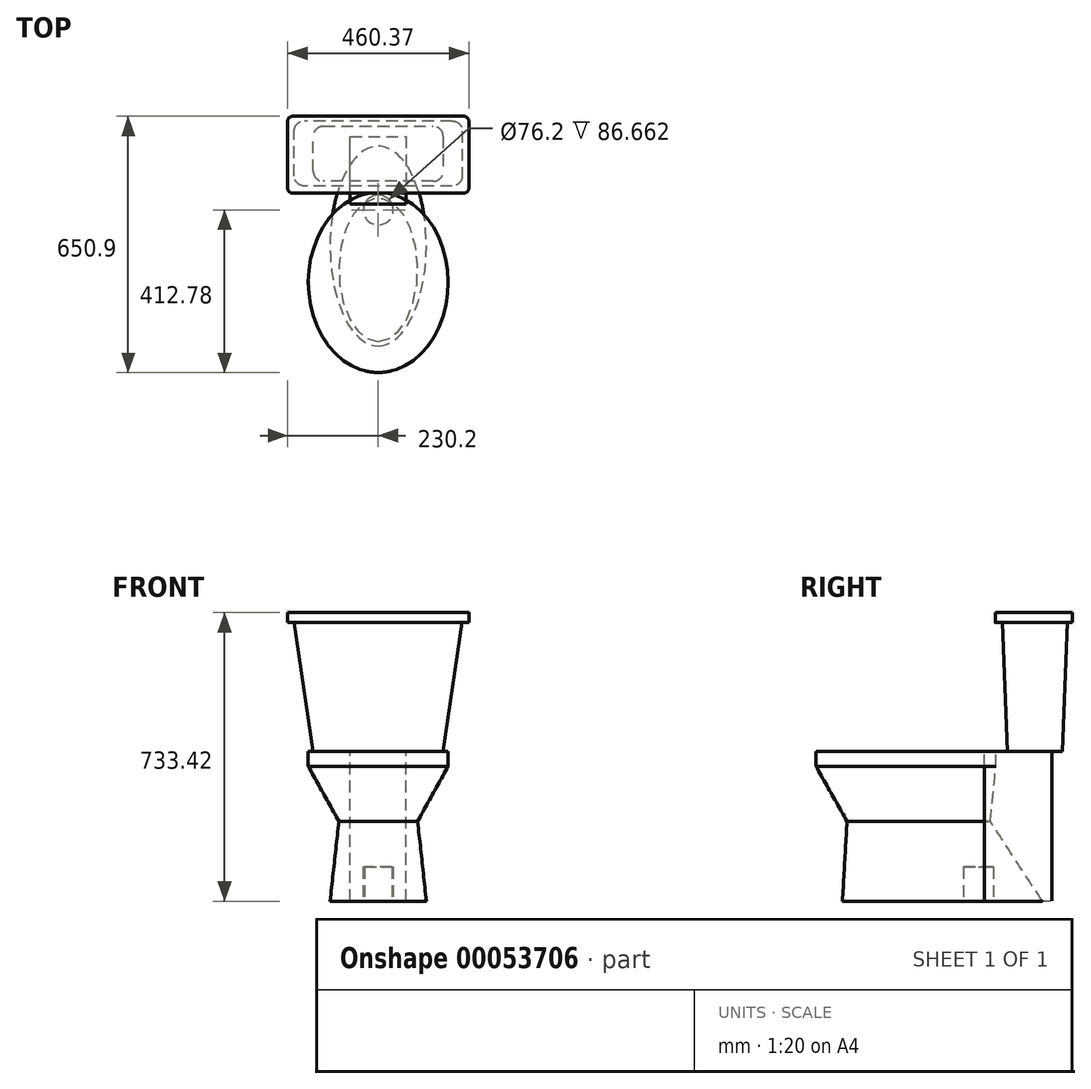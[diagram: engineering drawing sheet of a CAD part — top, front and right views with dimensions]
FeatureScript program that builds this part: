
annotation { "Feature Type Name" : "Feature", "Feature Type Description" : "" }
export const myFeature = defineFeature(function(context is Context, id is Id, definition is map)
    precondition{}
    {
        {
            var Q0;
            Q0=qCreatedBy(makeId("Top.planeOp"),FACE);
            var sketch = newSketch(context, id + "F0", { "sketchPlane" : qUnion([Q0])});
            skEllipse(sketch, "E0", {"center": v(0, 0) * mm, "majorRadius": 254 * mm, "minorRadius": 122.24 * mm, "majorAxis": v(0, 1)});
            skSolve(sketch);
        }
        {
            var Q0;
            Q0=makeQuery(id+"F0.imprint","IMPRINT",FACE,{"disambiguationData":[TD([[makeQuery(id+"F0.imprint","IMPRINT",EDGE,{"derivedFrom":sQuery(id+"F0.wireOp",EDGE,"E0")}),1.0]])]});
            cPlane(context, id + "F1", {"entities" : qUnion([Q0]), "cplaneType" : CPlaneType.OFFSET, "offset" : 203.2 * mm, "width" : 152.4 * mm, "height" : 152.4 * mm});
        }
        {
            var Q0;
            Q0=qCreatedBy(id+"F1.planeOp",FACE);
            var sketch = newSketch(context, id + "F2", { "sketchPlane" : qUnion([Q0])});
            skEllipse(sketch, "E1", {"center": v(0, -60.5) * mm, "majorRadius": 181.85 * mm, "minorRadius": 100.02 * mm, "majorAxis": v(0, -1)});
            skSolve(sketch);
        }
        {
            var Q0;
            Q0=makeQuery(id+"F2.imprint","IMPRINT",FACE,{"disambiguationData":[TD([[makeQuery(id+"F2.imprint","IMPRINT",EDGE,{"derivedFrom":sQuery(id+"F2.wireOp",EDGE,"E1")}),1.0]])]});
            var Q1;
            Q1=makeQuery(id+"F0.imprint","IMPRINT",FACE,{"disambiguationData":[TD([[makeQuery(id+"F0.imprint","IMPRINT",EDGE,{"derivedFrom":sQuery(id+"F0.wireOp",EDGE,"E0")}),1.0]])]});
            loft(context, id + "F3", {"sheetProfilesArray" : [{ "sheetProfileEntities" : qUnion([Q0]) }, { "sheetProfileEntities" : qUnion([Q1]) }]});
        }
        {
            var Q0;
            Q0=makeQuery(id+"F3.opLoft","CAP_FACE",FACE,{"disambiguationData":[OSD([makeQuery(id+"F0.imprint","IMPRINT",FACE,{"disambiguationData":[TD([[makeQuery(id+"F0.imprint","IMPRINT",EDGE,{"derivedFrom":sQuery(id+"F0.wireOp",EDGE,"E0")}),1.0]])]})])],"isStart":true});
            cPlane(context, id + "F4", {"entities" : qUnion([Q0]), "cplaneType" : CPlaneType.OFFSET, "offset" : 381 * mm, "oppositeDirection" : true, "width" : 152.4 * mm, "height" : 152.4 * mm});
        }
        {
            var Q0;
            Q0=qCreatedBy(id+"F4.planeOp",FACE);
            var sketch = newSketch(context, id + "F5", { "sketchPlane" : qUnion([Q0])});
            skEllipse(sketch, "E2", {"center": v(0, 92.74) * mm, "majorRadius": 228.6 * mm, "minorRadius": 177.8 * mm, "majorAxis": v(0, 1)});
            skSolve(sketch);
        }
        {
            var Q0;
            Q0=makeQuery(id+"F5.imprint","IMPRINT",FACE,{"disambiguationData":[TD([[makeQuery(id+"F5.imprint","IMPRINT",EDGE,{"derivedFrom":sQuery(id+"F5.wireOp",EDGE,"E2")}),1.0]])]});
            extrude(context, id + "F6", {"entities" : qUnion([Q0]), "depth" : 38.1 * mm});
        }
        {
            var Q1;
            Q1=makeQuery(id+"F6.opExtrude","CAP_FACE",FACE,{"disambiguationData":[OSD([sQuery(id+"F5.wireOp",EDGE,"E2")])],"isStart":false});
            var Q2;
            Q2=makeQuery(id+"F3.opLoft","CAP_FACE",FACE,{"disambiguationData":[OSD([makeQuery(id+"F2.imprint","IMPRINT",FACE,{"disambiguationData":[TD([[makeQuery(id+"F2.imprint","IMPRINT",EDGE,{"derivedFrom":sQuery(id+"F2.wireOp",EDGE,"E1")}),1.0]])]})])],"isStart":true});
            loft(context, id + "F7", {"operationType" : NewBodyOperationType.ADD, "sheetProfilesArray" : [{ "sheetProfileEntities" : qUnion([Q1]) }, { "sheetProfileEntities" : qUnion([Q2]) }]});
        }
        {
            var Q0;
            Q0=qCreatedBy(makeId("Front.planeOp"),FACE);
            cPlane(context, id + "F8", {"entities" : qUnion([Q0]), "cplaneType" : CPlaneType.OFFSET, "offset" : 345.44 * mm, "oppositeDirection" : true, "width" : 152.4 * mm, "height" : 152.4 * mm});
        }
        {
            var Q0;
            Q0=makeQuery(id+"F6.opExtrude","CAP_FACE",FACE,{"disambiguationData":[OSD([sQuery(id+"F5.wireOp",EDGE,"E2")])],"isStart":true});
            var sketch = newSketch(context, id + "F9", { "sketchPlane" : qUnion([Q0])});
            skLineSegment(sketch, "E3", {"start": v(0, -92.74) * mm, "end": v(0, -360.2) * mm, "construction": true});
            skPoint(sketch, "E3.endSnap0", {"position": v(0, -321.34) * mm});
            skSolve(sketch);
        }
        {
            var Q0;
            Q0=qCreatedBy(id+"F8.planeOp",FACE);
            cPlane(context, id + "F10", {"entities" : qUnion([Q0]), "cplaneType" : CPlaneType.OFFSET, "offset" : 15.88 * mm, "width" : 152.4 * mm, "height" : 152.4 * mm});
        }
        {
            var Q0;
            Q0=makeQuery(id+"F3.opLoft","CAP_FACE",FACE,{"disambiguationData":[OSD([makeQuery(id+"F0.imprint","IMPRINT",FACE,{"disambiguationData":[TD([[makeQuery(id+"F0.imprint","IMPRINT",EDGE,{"derivedFrom":sQuery(id+"F0.wireOp",EDGE,"E0")}),1.0]])]})])],"isStart":true});
            var sketch = newSketch(context, id + "F11", { "sketchPlane" : qUnion([Q0])});
            skLineSegment(sketch, "E4", {"start": v(0, 0) * mm, "end": v(0, -417.16) * mm, "construction": true});
            skSolve(sketch);
        }
        {
            var Q0;
            Q0=makeQuery(id+"F11.imprint","IMPRINT",FACE,{"disambiguationData":[TD([[makeQuery(id+"F11.imprint","IMPRINT",EDGE,{"derivedFrom":makeQuery(id+"F3.opLoft","MID_CAP_EDGE",EDGE,{"disambiguationData":[OSD([sQuery(id+"F0.wireOp",EDGE,"E0"),sQuery(id+"F2.wireOp",EDGE,"E1")])],"capPos":1.0})}),1.0]])]});
            cPlane(context, id + "F12", {"entities" : qUnion([Q0]), "cplaneType" : CPlaneType.OFFSET, "offset" : 733.42 * mm, "oppositeDirection" : true, "width" : 152.4 * mm, "height" : 152.4 * mm});
        }
        {
            var Q0;
            Q0=qCreatedBy(id+"F12.planeOp",FACE);
            var sketch = newSketch(context, id + "F13", { "sketchPlane" : qUnion([Q0])});
            skPoint(sketch, "E5", {"position": v(0, -329.56) * mm});
            skSolve(sketch);
        }
        {
            var Q0;
            Q0=qCreatedBy(id+"F12.planeOp",FACE);
            var sketch = newSketch(context, id + "F14", { "sketchPlane" : qUnion([Q0])});
            skLineSegment(sketch, "E6", {"start": v(0, -329.56) * mm, "end": v(230.17, -329.56) * mm});
            skLineSegment(sketch, "E7", {"start": v(230.17, -329.56) * mm, "end": v(230.17, -134.29) * mm});
            skLineSegment(sketch, "E8", {"start": v(230.17, -134.29) * mm, "end": v(-230.2, -134.29) * mm});
            skLineSegment(sketch, "E9", {"start": v(-230.2, -134.29) * mm, "end": v(-230.2, -329.56) * mm});
            skLineSegment(sketch, "E10", {"start": v(0, -329.56) * mm, "end": v(-230.2, -329.56) * mm});
            skSolve(sketch);
        }
        {
            var Q0;
            Q0=makeQuery(id+"F14.imprint","IMPRINT",FACE,{"disambiguationData":[TD([[makeQuery(id+"F14.imprint","IMPRINT",EDGE,{"derivedFrom":sQuery(id+"F14.wireOp",EDGE,"E6")}),1.0]])]});
            extrude(context, id + "F15", {"entities" : qUnion([Q0]), "depth" : 25.4 * mm});
        }
        {
            var Q0;
            Q0=makeQuery(id+"F15.opExtrude","SWEPT_EDGE",EDGE,{"disambiguationData":[OSD([sQuery(id+"F14.wireOp",EDGE,"E7"),sQuery(id+"F14.wireOp",EDGE,"E8")])]});
            var Q1;
            Q1=makeQuery(id+"F15.opExtrude","SWEPT_EDGE",EDGE,{"disambiguationData":[OSD([sQuery(id+"F14.wireOp",EDGE,"E8"),sQuery(id+"F14.wireOp",EDGE,"E9")])]});
            var Q2;
            Q2=makeQuery(id+"F15.opExtrude","SWEPT_EDGE",EDGE,{"disambiguationData":[OSD([sQuery(id+"F14.wireOp",EDGE,"E6"),sQuery(id+"F14.wireOp",EDGE,"E7")])]});
            var Q3;
            Q3=makeQuery(id+"F15.opExtrude","SWEPT_EDGE",EDGE,{"disambiguationData":[OSD([sQuery(id+"F14.wireOp",EDGE,"E9"),sQuery(id+"F14.wireOp",EDGE,"E10")])]});
            fillet(context, id + "F16", {"entities" : qUnion([Q0, Q1, Q2, Q3]), "radius" : 12.7 * mm, "tangentPropagation" : true, "allowEdgeOverflow" : false});
        }
        {
            var Q0;
            Q0=makeQuery(id+"F9.imprint","IMPRINT",FACE,{"disambiguationData":[TD([[makeQuery(id+"F9.imprint","IMPRINT",EDGE,{"derivedFrom":makeQuery(id+"F6.opExtrude","CAP_EDGE",EDGE,{"disambiguationData":[OSD([sQuery(id+"F5.wireOp",EDGE,"E2")])],"isStart":true})}),-1.0]])]});
            var sketch = newSketch(context, id + "F17", { "sketchPlane" : qUnion([Q0])});
            skLineSegment(sketch, "E11", {"start": v(-165.1, 304.16) * mm, "end": v(0, 304.16) * mm});
            skLineSegment(sketch, "E12", {"start": v(0, 304.16) * mm, "end": v(165.1, 304.16) * mm});
            skLineSegment(sketch, "E13", {"start": v(165.1, 304.16) * mm, "end": v(165.1, 164.46) * mm});
            skLineSegment(sketch, "E14", {"start": v(165.1, 164.46) * mm, "end": v(-165.1, 164.46) * mm});
            skLineSegment(sketch, "E15", {"start": v(-165.1, 164.46) * mm, "end": v(-165.1, 304.16) * mm});
            skSolve(sketch);
        }
        {
            var Q0;
            Q0=makeQuery(id+"F15.opExtrude","CAP_FACE",FACE,{"disambiguationData":[OSD([sQuery(id+"F14.wireOp",EDGE,"E6"),sQuery(id+"F14.wireOp",EDGE,"E7"),sQuery(id+"F14.wireOp",EDGE,"E8"),sQuery(id+"F14.wireOp",EDGE,"E9"),sQuery(id+"F14.wireOp",EDGE,"E10")])],"isStart":false});
            var sketch = newSketch(context, id + "F18", { "sketchPlane" : qUnion([Q0])});
            skLineSegment(sketch, "E16", {"start": v(0, -317.7) * mm, "end": v(213.36, -317.7) * mm});
            skLineSegment(sketch, "E17", {"start": v(213.36, -317.7) * mm, "end": v(213.36, -152.6) * mm});
            skLineSegment(sketch, "E18", {"start": v(213.36, -152.6) * mm, "end": v(-213.36, -152.6) * mm});
            skLineSegment(sketch, "E19", {"start": v(-213.36, -152.6) * mm, "end": v(-213.36, -317.7) * mm});
            skLineSegment(sketch, "E20", {"start": v(0, -317.7) * mm, "end": v(-213.36, -317.7) * mm});
            skSolve(sketch);
        }
        {
            var Q1;
            Q1=makeQuery(id+"F18.imprint","IMPRINT",FACE,{"disambiguationData":[TD([[makeQuery(id+"F18.imprint","IMPRINT",EDGE,{"derivedFrom":sQuery(id+"F18.wireOp",EDGE,"E16")}),1.0]])]});
            var Q2;
            Q2=makeQuery(id+"F17.imprint","IMPRINT",FACE,{"disambiguationData":[TD([[makeQuery(id+"F17.imprint","IMPRINT",EDGE,{"derivedFrom":sQuery(id+"F17.wireOp",EDGE,"E11")}),-1.0]])]});
            loft(context, id + "F19", {"operationType" : NewBodyOperationType.ADD, "sheetProfilesArray" : [{ "sheetProfileEntities" : qUnion([Q1]) }, { "sheetProfileEntities" : qUnion([Q2]) }]});
        }
        {
            var Q0;
            Q0=makeQuery(id+"F19.opLoft","CAP_FACE",FACE,{"disambiguationData":[OSD([makeQuery(id+"F17.imprint","IMPRINT",FACE,{"disambiguationData":[TD([[makeQuery(id+"F17.imprint","IMPRINT",EDGE,{"derivedFrom":sQuery(id+"F17.wireOp",EDGE,"E11")}),-1.0]])]})])],"isStart":true});
            var sketch = newSketch(context, id + "F20", { "sketchPlane" : qUnion([Q0])});
            skLineSegment(sketch, "E21", {"start": v(0, -278.52) * mm, "end": v(71.12, -278.52) * mm});
            skLineSegment(sketch, "E22", {"start": v(71.12, -278.52) * mm, "end": v(71.12, -106.79) * mm});
            skLineSegment(sketch, "E23", {"start": v(71.12, -106.79) * mm, "end": v(-71.12, -106.79) * mm});
            skLineSegment(sketch, "E24", {"start": v(-71.12, -106.79) * mm, "end": v(-71.12, -278.52) * mm});
            skLineSegment(sketch, "E25", {"start": v(0, -278.52) * mm, "end": v(-71.12, -278.52) * mm});
            skSolve(sketch);
        }
        {
            var Q0;
            {var subQ0=sQuery(id+"F20.wireOp",EDGE,"E23");Q0=makeQuery(id+"F20.imprint","IMPRINT",FACE,{"disambiguationData":[TD([[makeQuery(id+"F20.imprint","IMPRINT",EDGE,{"derivedFrom":subQ0}),1.0]])]});}
            var Q1;
            {var subQ5=sQuery(id+"F20.wireOp",EDGE,"E21");Q1=makeQuery(id+"F20.imprint","IMPRINT",FACE,{"disambiguationData":[TD([[makeQuery(id+"F20.imprint","IMPRINT",EDGE,{"derivedFrom":subQ5}),1.0]])]});}
            extrude(context, id + "F21", {"entities" : qUnion([Q0, Q1]), "depth" : 380.43 * mm});
        }
        {
            var Q0;
            Q0=makeQuery(id+"F11.imprint","IMPRINT",FACE,{"disambiguationData":[TD([[makeQuery(id+"F11.imprint","IMPRINT",EDGE,{"derivedFrom":makeQuery(id+"F3.opLoft","MID_CAP_EDGE",EDGE,{"disambiguationData":[OSD([sQuery(id+"F0.wireOp",EDGE,"E0"),sQuery(id+"F2.wireOp",EDGE,"E1")])],"capPos":1.0})}),1.0]])]});
            var sketch = newSketch(context, id + "F22", { "sketchPlane" : qUnion([Q0])});
            skCircle(sketch, "E26", {"center": v(0, -91.44) * mm, "radius": 38.1 * mm});
            skSolve(sketch);
        }
        {
            var Q0;
            Q0 = qSketchRegion(id + "F22", true);
            extrude(context, id + "F23", {"entities" : qUnion([Q0]), "operationType" : NewBodyOperationType.REMOVE, "oppositeDirection" : true, "depth" : 86.66 * mm});
        }
        {
            var Q0;
            Q0=makeQuery(id+"F19.opLoft","SWEPT_EDGE",EDGE,{"disambiguationData":[OSD([sQuery(id+"F17.wireOp",EDGE,"E13"),sQuery(id+"F17.wireOp",EDGE,"E14"),sQuery(id+"F18.wireOp",EDGE,"E17"),sQuery(id+"F18.wireOp",EDGE,"E18")])]});
            var Q1;
            Q1=makeQuery(id+"F19.opLoft","SWEPT_EDGE",EDGE,{"disambiguationData":[OSD([sQuery(id+"F17.wireOp",EDGE,"E12"),sQuery(id+"F17.wireOp",EDGE,"E13"),sQuery(id+"F18.wireOp",EDGE,"E16"),sQuery(id+"F18.wireOp",EDGE,"E17")])]});
            var Q2;
            Q2=makeQuery(id+"F19.opLoft","SWEPT_EDGE",EDGE,{"disambiguationData":[OSD([sQuery(id+"F17.wireOp",EDGE,"E14"),sQuery(id+"F17.wireOp",EDGE,"E15"),sQuery(id+"F18.wireOp",EDGE,"E18"),sQuery(id+"F18.wireOp",EDGE,"E19")])]});
            var Q3;
            Q3=makeQuery(id+"F19.opLoft","SWEPT_EDGE",EDGE,{"disambiguationData":[OSD([sQuery(id+"F17.wireOp",EDGE,"E11"),sQuery(id+"F17.wireOp",EDGE,"E15"),sQuery(id+"F18.wireOp",EDGE,"E19"),sQuery(id+"F18.wireOp",EDGE,"E20")])]});
            fillet(context, id + "F24", {"entities" : qUnion([Q0, Q1, Q2, Q3]), "radius" : 25.4 * mm, "tangentPropagation" : true, "allowEdgeOverflow" : false});
        }
    });
